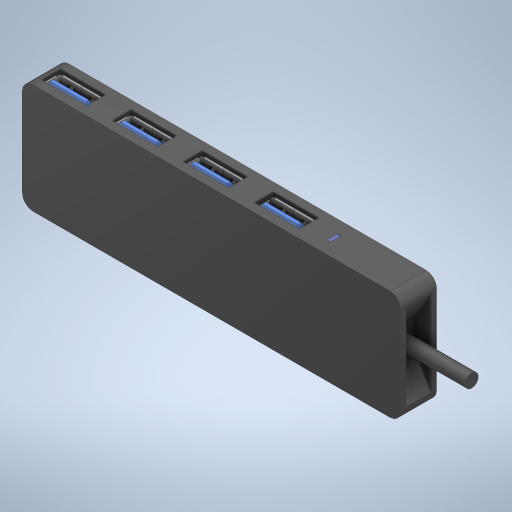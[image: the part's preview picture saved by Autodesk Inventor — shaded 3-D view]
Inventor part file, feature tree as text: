
AUTODESK INVENTOR PART (.ipt)
format: ipt  version: 2024.2 (Build 282272000, 272)  size: 4,744,192 bytes
history: native  units: mm
features: other x50, plane x2
ambient origin geometry x8: Origin, YZ Plane, XZ Plane, XY Plane, X Axis, Y Axis, Z Axis, Center Point
bodies: Solid1 (feature_tree), Solid2 (feature_tree), Solid3 (feature_tree), Solid4 (feature_tree), Solid5 (feature_tree), Solid6 (feature_tree), Solid7 (feature_tree), Solid8 (feature_tree), Solid9 (feature_tree), Solid10 (feature_tree), Solid11 (feature_tree), Solid12 (feature_tree), Solid13 (feature_tree), Solid14 (feature_tree), Solid15 (feature_tree), Solid16 (feature_tree), Solid17 (feature_tree), Solid18 (feature_tree), Solid19 (feature_tree), Solid20 (feature_tree), Solid21 (feature_tree), Solid22 (feature_tree), Solid23 (feature_tree), Solid24 (feature_tree), Solid25 (feature_tree), Solid26 (feature_tree), Solid27 (feature_tree), Solid28 (feature_tree), Solid29 (feature_tree), Solid30 (feature_tree), Solid31 (feature_tree), Solid32 (feature_tree), Solid33 (feature_tree), Solid34 (feature_tree), Solid35 (feature_tree), Solid36 (feature_tree), Solid37 (feature_tree), Solid38 (feature_tree), Solid39 (feature_tree), Solid40 (feature_tree), Solid41 (feature_tree), Solid42 (feature_tree), Solid43 (feature_tree), Solid44 (feature_tree), Solid45 (feature_tree), Solid46 (feature_tree), Solid47 (feature_tree), Solid48 (feature_tree), Solid49 (feature_tree)
feature tree (52):
  other  "ANKER 4 PORT USB HUB v2.iam"
  other  "USB 3.0 Тип A Вертикальный v1.iam:1::USB 3.ipt:1"
  other  "USB 3.0 Тип A Вертикальный v1.iam:1::USB 3 (1).ipt:1"
  other  "USB 3.0 Тип A Вертикальный v1.iam:1::USB 3 (2).ipt:1"
  other  "USB 3.0 Тип A Вертикальный v1.iam:1::USB 3 (3).ipt:1"
  other  "USB 3.0 Тип A Вертикальный v1.iam:1::USB 3 (4).ipt:1"
  other  "USB 3.0 Тип A Вертикальный v1.iam:1::USB 3 (3).ipt:2"
  other  "USB 3.0 Тип A Вертикальный v1.iam:1::USB 3 (3).ipt:3"
  other  "USB 3.0 Тип A Вертикальный v1.iam:1::USB 3 (3).ipt:4"
  other  "USB 3.0 Тип A Вертикальный v1.iam:1::USB 3 (3).ipt:5"
  other  "USB 3.0 Тип A Вертикальный v1.iam:1::USB 3 (4).ipt:2"
  other  "USB 3.0 Тип A Вертикальный v1.iam:1::USB 3 (4).ipt:3"
  other  "USB 3.0 Тип A Вертикальный v1.iam:1::USB 3 (4).ipt:4"
  other  "USB 3.0 Тип A Вертикальный v1.iam:2::USB 3.ipt:1"
  other  "USB 3.0 Тип A Вертикальный v1.iam:2::USB 3 (1).ipt:1"
  other  "USB 3.0 Тип A Вертикальный v1.iam:2::USB 3 (2).ipt:1"
  other  "USB 3.0 Тип A Вертикальный v1.iam:2::USB 3 (3).ipt:1"
  other  "USB 3.0 Тип A Вертикальный v1.iam:2::USB 3 (4).ipt:1"
  other  "USB 3.0 Тип A Вертикальный v1.iam:2::USB 3 (3).ipt:2"
  other  "USB 3.0 Тип A Вертикальный v1.iam:2::USB 3 (3).ipt:3"
  other  "USB 3.0 Тип A Вертикальный v1.iam:2::USB 3 (3).ipt:4"
  other  "USB 3.0 Тип A Вертикальный v1.iam:2::USB 3 (3).ipt:5"
  other  "USB 3.0 Тип A Вертикальный v1.iam:2::USB 3 (4).ipt:2"
  other  "USB 3.0 Тип A Вертикальный v1.iam:2::USB 3 (4).ipt:3"
  other  "USB 3.0 Тип A Вертикальный v1.iam:2::USB 3 (4).ipt:4"
  other  "USB 3.0 Тип A Вертикальный v1.iam:3::USB 3.ipt:1"
  other  "USB 3.0 Тип A Вертикальный v1.iam:3::USB 3 (1).ipt:1"
  other  "USB 3.0 Тип A Вертикальный v1.iam:3::USB 3 (2).ipt:1"
  other  "USB 3.0 Тип A Вертикальный v1.iam:3::USB 3 (3).ipt:1"
  other  "USB 3.0 Тип A Вертикальный v1.iam:3::USB 3 (4).ipt:1"
  other  "USB 3.0 Тип A Вертикальный v1.iam:3::USB 3 (3).ipt:2"
  other  "USB 3.0 Тип A Вертикальный v1.iam:3::USB 3 (3).ipt:3"
  other  "USB 3.0 Тип A Вертикальный v1.iam:3::USB 3 (3).ipt:4"
  other  "USB 3.0 Тип A Вертикальный v1.iam:3::USB 3 (3).ipt:5"
  other  "USB 3.0 Тип A Вертикальный v1.iam:3::USB 3 (4).ipt:2"
  other  "USB 3.0 Тип A Вертикальный v1.iam:3::USB 3 (4).ipt:3"
  other  "USB 3.0 Тип A Вертикальный v1.iam:3::USB 3 (4).ipt:4"
  other  "USB 3.0 Тип A Вертикальный v1.iam:4::USB 3.ipt:1"
  other  "USB 3.0 Тип A Вертикальный v1.iam:4::USB 3 (1).ipt:1"
  other  "USB 3.0 Тип A Вертикальный v1.iam:4::USB 3 (2).ipt:1"
  other  "USB 3.0 Тип A Вертикальный v1.iam:4::USB 3 (3).ipt:1"
  other  "USB 3.0 Тип A Вертикальный v1.iam:4::USB 3 (4).ipt:1"
  other  "USB 3.0 Тип A Вертикальный v1.iam:4::USB 3 (3).ipt:2"
  other  "USB 3.0 Тип A Вертикальный v1.iam:4::USB 3 (3).ipt:3"
  other  "USB 3.0 Тип A Вертикальный v1.iam:4::USB 3 (3).ipt:4"
  other  "USB 3.0 Тип A Вертикальный v1.iam:4::USB 3 (3).ipt:5"
  other  "USB 3.0 Тип A Вертикальный v1.iam:4::USB 3 (4).ipt:2"
  other  "USB 3.0 Тип A Вертикальный v1.iam:4::USB 3 (4).ipt:3"
  other  "USB 3.0 Тип A Вертикальный v1.iam:4::USB 3 (4).ipt:4"
  other  "Part13.ipt:1"
  plane  "Work Plane1"
  plane  "Work Plane2"
